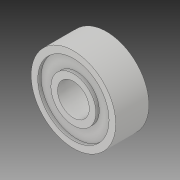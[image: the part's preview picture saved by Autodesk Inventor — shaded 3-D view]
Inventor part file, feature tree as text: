
AUTODESK INVENTOR PART (.ipt)
format: ipt  version: 2019 (Build 230136000, 136)  size: 120,832 bytes
history: native  units: in
note: dims shown in document units (in); Inventor stores cm internally (conversion verified against a paired STEP export)
features: revolve x1
ambient origin geometry x8: Origin, YZ Plane, XZ Plane, XY Plane, X Axis, Y Axis, Z Axis, Center Point
bodies: Solid1 (feature_tree)
feature tree (1):
  revolve  "Revolve1"  [1 undecoded]
note: 1 required parameter value undecoded (feature->parameter linkage not recoverable at this tier; creation-order binding heuristic only, values carry confidence <= 0.55)
